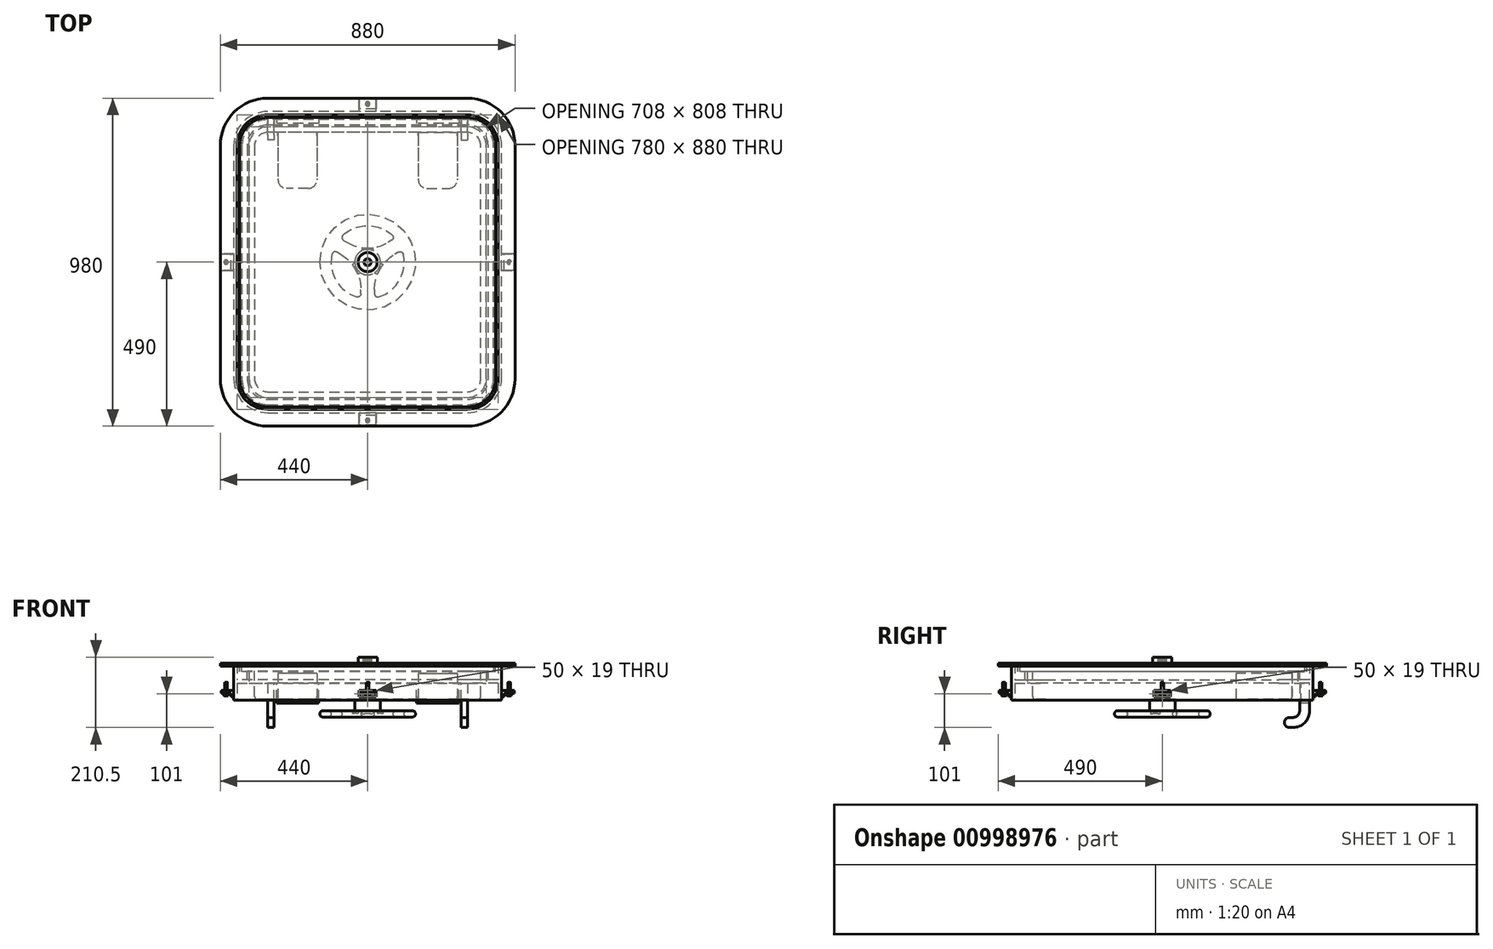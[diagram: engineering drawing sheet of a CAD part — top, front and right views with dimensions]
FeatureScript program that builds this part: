
annotation { "Feature Type Name" : "Feature", "Feature Type Description" : "" }
export const myFeature = defineFeature(function(context is Context, id is Id, definition is map)
    precondition{}
    {
        {
            var Q0;
            Q0=qCreatedBy(makeId("Top.planeOp"),FACE);
            var sketch = newSketch(context, id + "F0", { "sketchPlane" : qUnion([Q0])});
            skLineSegment(sketch, "E0.bottom", {"start": v(-298.4, -450) * mm, "end": v(298.4, -450) * mm});
            skLineSegment(sketch, "E0.top", {"start": v(-298.4, 450) * mm, "end": v(298.4, 450) * mm});
            skLineSegment(sketch, "E0.left", {"start": v(-400, -348.4) * mm, "end": v(-400, 348.4) * mm});
            skLineSegment(sketch, "E0.right", {"start": v(400, -348.4) * mm, "end": v(400, 348.4) * mm});
            skPoint(sketch, "E0.middle", {"position": v(0, 0) * mm});
            skPoint(sketch, "E1.visualSharp", {"position": v(-400, 450) * mm});
            skArc(sketch, "E1.filletArc", {"start": v(-298.4, 450) * mm, "mid": v(-370.24, 420.24) * mm, "end": v(-400, 348.4) * mm});
            skPoint(sketch, "E2.visualSharp", {"position": v(400, 450) * mm});
            skArc(sketch, "E2.filletArc", {"start": v(400, 348.4) * mm, "mid": v(370.24, 420.24) * mm, "end": v(298.4, 450) * mm});
            skPoint(sketch, "E3.visualSharp", {"position": v(400, -450) * mm});
            skArc(sketch, "E3.filletArc", {"start": v(298.4, -450) * mm, "mid": v(370.24, -420.24) * mm, "end": v(400, -348.4) * mm});
            skPoint(sketch, "E4.visualSharp", {"position": v(-400, -450) * mm});
            skArc(sketch, "E4.filletArc", {"start": v(-400, -348.4) * mm, "mid": v(-370.24, -420.24) * mm, "end": v(-298.4, -450) * mm});
            skSolve(sketch);
        }
        {
            var Q0;
            Q0=qCreatedBy(makeId("Front.planeOp"),FACE);
            var sketch = newSketch(context, id + "F1", { "sketchPlane" : qUnion([Q0])});
            skLineSegment(sketch, "E5", {"start": v(-400, 0) * mm, "end": v(-440, 0) * mm});
            skLineSegment(sketch, "E6", {"start": v(-440, 0) * mm, "end": v(-440, 8) * mm});
            skLineSegment(sketch, "E7", {"start": v(-440, 8) * mm, "end": v(-390, 8) * mm});
            skLineSegment(sketch, "E8", {"start": v(-390, 8) * mm, "end": v(-390, -41) * mm});
            skLineSegment(sketch, "E9", {"start": v(-390, -41) * mm, "end": v(-360, -41) * mm});
            skLineSegment(sketch, "E10", {"start": v(-360, -41) * mm, "end": v(-360, -16) * mm});
            skLineSegment(sketch, "E11", {"start": v(-360, -16) * mm, "end": v(-354, -16) * mm});
            skLineSegment(sketch, "E12", {"start": v(-354, -16) * mm, "end": v(-354, -51) * mm});
            skLineSegment(sketch, "E13", {"start": v(-354, -51) * mm, "end": v(-390, -51) * mm});
            skLineSegment(sketch, "E14", {"start": v(-390, -51) * mm, "end": v(-390, -102) * mm});
            skLineSegment(sketch, "E15", {"start": v(-390, -102) * mm, "end": v(-400, -102) * mm});
            skLineSegment(sketch, "E16", {"start": v(-400, -102) * mm, "end": v(-400, 0) * mm});
            skSolve(sketch);
        }
        {
            var Q0;
            Q0=makeQuery(id+"F1.imprint","IMPRINT",FACE,{"disambiguationData":[TD([[makeQuery(id+"F1.imprint","IMPRINT",EDGE,{"derivedFrom":sQuery(id+"F1.wireOp",EDGE,"E5")}),-1.0]])]});
            var Q1;
            Q1=sQuery(id+"F0.wireOp",EDGE,"E0.left");
            var Q2;
            Q2=sQuery(id+"F0.wireOp",EDGE,"E1.filletArc");
            var Q3;
            Q3=sQuery(id+"F0.wireOp",EDGE,"E0.top");
            var Q4;
            Q4=sQuery(id+"F0.wireOp",EDGE,"E2.filletArc");
            var Q5;
            Q5=sQuery(id+"F0.wireOp",EDGE,"E0.right");
            var Q6;
            Q6=sQuery(id+"F0.wireOp",EDGE,"E3.filletArc");
            var Q7;
            Q7=sQuery(id+"F0.wireOp",EDGE,"E0.bottom");
            var Q8;
            Q8=sQuery(id+"F0.wireOp",EDGE,"E4.filletArc");
            sweep(context, id + "F2", {"profiles" : qUnion([Q0]), "path" : qUnion([Q1, Q2, Q3, Q4, Q5, Q6, Q7, Q8])});
        }
        {
            var Q0;
            Q0=makeQuery(id+"F2.opSweep","SWEPT_FACE",FACE,{"disambiguationData":[OSD([sQuery(id+"F0.wireOp",EDGE,"E0.left"),sQuery(id+"F1.wireOp",EDGE,"E7")])]});
            var sketch = newSketch(context, id + "F3", { "sketchPlane" : qUnion([Q0])});
            skLineSegment(sketch, "E17.0", {"start": v(298.4, 432) * mm, "end": v(-298.4, 432) * mm});
            skArc(sketch, "E17.1", {"start": v(382, 348.4) * mm, "mid": v(357.51, 407.51) * mm, "end": v(298.4, 432) * mm});
            skArc(sketch, "E17.2", {"start": v(-298.4, 432) * mm, "mid": v(-357.51, 407.51) * mm, "end": v(-382, 348.4) * mm});
            skLineSegment(sketch, "E17.3", {"start": v(382, -348.4) * mm, "end": v(382, 348.4) * mm});
            skLineSegment(sketch, "E17.4", {"start": v(-382, 348.4) * mm, "end": v(-382, -348.4) * mm});
            skArc(sketch, "E17.5", {"start": v(-382, -348.4) * mm, "mid": v(-357.51, -407.51) * mm, "end": v(-298.4, -432) * mm});
            skLineSegment(sketch, "E17.6", {"start": v(-298.4, -432) * mm, "end": v(298.4, -432) * mm});
            skArc(sketch, "E17.7", {"start": v(298.4, -432) * mm, "mid": v(357.51, -407.51) * mm, "end": v(382, -348.4) * mm});
            skSolve(sketch);
        }
        {
            var Q0;
            Q0=qSketchRegion(id+"F3",true);
            extrude(context, id + "F4", {"entities" : qUnion([Q0]), "oppositeDirection" : true, "depth" : 25 * mm, "offsetDistance" : 25 * mm});
        }
        {
            var Q0;
            Q0=makeQuery(id+"F4.opExtrude","CAP_FACE",FACE,{"disambiguationData":[OSD([sQuery(id+"F3.wireOp",EDGE,"E17.0"),sQuery(id+"F3.wireOp",EDGE,"E17.1"),sQuery(id+"F3.wireOp",EDGE,"E17.2"),sQuery(id+"F3.wireOp",EDGE,"E17.3"),sQuery(id+"F3.wireOp",EDGE,"E17.4"),sQuery(id+"F3.wireOp",EDGE,"E17.5"),sQuery(id+"F3.wireOp",EDGE,"E17.6"),sQuery(id+"F3.wireOp",EDGE,"E17.7")])],"isStart":false});
            shell(context, id + "F5", {"entities" : qUnion([Q0]), "thickness" : 6.35 * mm});
        }
        {
            var Q0;
            Q0=makeQuery(id+"F4.opExtrude","CAP_EDGE",EDGE,{"disambiguationData":[OSD([sQuery(id+"F3.wireOp",EDGE,"E17.6")])],"isStart":true});
            fillet(context, id + "F6", {"entities" : qUnion([Q0]), "radius" : 12.7 * mm, "tangentPropagation" : true, "allowEdgeOverflow" : false});
        }
        {
            var Q0;
            Q0=makeQuery(id+"F5.opShell","OFFSET_FACE",FACE,{"disambiguationData":[OSD([sQuery(id+"F3.wireOp",EDGE,"E17.0"),sQuery(id+"F3.wireOp",EDGE,"E17.1"),sQuery(id+"F3.wireOp",EDGE,"E17.2"),sQuery(id+"F3.wireOp",EDGE,"E17.3"),sQuery(id+"F3.wireOp",EDGE,"E17.4"),sQuery(id+"F3.wireOp",EDGE,"E17.5"),sQuery(id+"F3.wireOp",EDGE,"E17.6"),sQuery(id+"F3.wireOp",EDGE,"E17.7")])]});
            var sketch = newSketch(context, id + "F7", { "sketchPlane" : qUnion([Q0])});
            skLineSegment(sketch, "E18.0", {"start": v(-337.55, -348.4) * mm, "end": v(-337.55, 348.4) * mm});
            skArc(sketch, "E18.1", {"start": v(-298.4, -387.55) * mm, "mid": v(-326.08, -376.08) * mm, "end": v(-337.55, -348.4) * mm});
            skArc(sketch, "E18.2", {"start": v(-337.55, 348.4) * mm, "mid": v(-326.08, 376.08) * mm, "end": v(-298.4, 387.55) * mm});
            skLineSegment(sketch, "E18.3", {"start": v(298.4, -387.55) * mm, "end": v(-298.4, -387.55) * mm});
            skLineSegment(sketch, "E18.4", {"start": v(-298.4, 387.55) * mm, "end": v(298.4, 387.55) * mm});
            skArc(sketch, "E18.5", {"start": v(298.4, 387.55) * mm, "mid": v(326.08, 376.08) * mm, "end": v(337.55, 348.4) * mm});
            skLineSegment(sketch, "E18.6", {"start": v(337.55, 348.4) * mm, "end": v(337.55, -348.4) * mm});
            skArc(sketch, "E18.7", {"start": v(337.55, -348.4) * mm, "mid": v(326.08, -376.08) * mm, "end": v(298.4, -387.55) * mm});
            skSolve(sketch);
        }
        {
            var Q0;
            Q0=qSketchRegion(id+"F7",true);
            extrude(context, id + "F8", {"entities" : qUnion([Q0]), "operationType" : NewBodyOperationType.ADD, "depth" : 101.6 * mm, "offsetDistance" : 25 * mm});
        }
        {
            var Q0;
            Q0=makeQuery(id+"F8.opExtrude","CAP_EDGE",EDGE,{"disambiguationData":[OSD([sQuery(id+"F7.wireOp",EDGE,"E18.0")])],"isStart":false});
            fillet(context, id + "F9", {"entities" : qUnion([Q0]), "radius" : 10 * mm, "tangentPropagation" : true, "allowEdgeOverflow" : false});
        }
        {
            var Q0;
            Q0=makeQuery(id+"F4.opExtrude","CAP_FACE",FACE,{"disambiguationData":[OSD([sQuery(id+"F3.wireOp",EDGE,"E17.0"),sQuery(id+"F3.wireOp",EDGE,"E17.1"),sQuery(id+"F3.wireOp",EDGE,"E17.2"),sQuery(id+"F3.wireOp",EDGE,"E17.3"),sQuery(id+"F3.wireOp",EDGE,"E17.4"),sQuery(id+"F3.wireOp",EDGE,"E17.5"),sQuery(id+"F3.wireOp",EDGE,"E17.6"),sQuery(id+"F3.wireOp",EDGE,"E17.7")])],"isStart":true});
            var sketch = newSketch(context, id + "F10", { "sketchPlane" : qUnion([Q0])});
            skCircle(sketch, "E19", {"center": v(0, 0) * mm, "radius": 28.6 * mm});
            skSolve(sketch);
        }
        {
            var Q0;
            Q0=qSketchRegion(id+"F10",true);
            extrude(context, id + "F11", {"entities" : qUnion([Q0]), "operationType" : NewBodyOperationType.ADD, "depth" : 19 * mm, "offsetDistance" : 25 * mm});
        }
        {
            var Q0;
            Q0=makeQuery(id+"F11.opExtrude","CAP_FACE",FACE,{"disambiguationData":[OSD([sQuery(id+"F10.wireOp",EDGE,"E19")])],"isStart":false});
            var sketch = newSketch(context, id + "F12", { "sketchPlane" : qUnion([Q0])});
            skLineSegment(sketch, "E20.bottom", {"start": v(8.75, -8.75) * mm, "end": v(3.62, -8.75) * mm});
            skLineSegment(sketch, "E20.top", {"start": v(8.75, 8.75) * mm, "end": v(3.62, 8.75) * mm});
            skLineSegment(sketch, "E20.left", {"start": v(8.75, -8.75) * mm, "end": v(8.75, -3.62) * mm});
            skLineSegment(sketch, "E20.right", {"start": v(-8.75, -8.75) * mm, "end": v(-8.75, -3.62) * mm});
            skPoint(sketch, "E20.middle", {"position": v(0, 0) * mm});
            skLineSegment(sketch, "E21.bottom", {"start": v(12.37, 0) * mm, "end": v(8.75, -3.62) * mm});
            skLineSegment(sketch, "E21.top", {"start": v(0, 12.37) * mm, "end": v(-3.62, 8.75) * mm});
            skLineSegment(sketch, "E21.left", {"start": v(12.37, 0) * mm, "end": v(8.75, 3.62) * mm});
            skLineSegment(sketch, "E21.right", {"start": v(0, -12.37) * mm, "end": v(-3.62, -8.75) * mm});
            skLineSegment(sketch, "E22.trimOffspring", {"start": v(-8.75, 3.62) * mm, "end": v(-12.37, 0) * mm});
            skLineSegment(sketch, "E23.trimOffspring", {"start": v(-8.75, 3.62) * mm, "end": v(-8.75, 8.75) * mm});
            skLineSegment(sketch, "E24.trimOffspring", {"start": v(-8.75, -3.62) * mm, "end": v(-12.37, 0) * mm});
            skLineSegment(sketch, "E25.trimOffspring", {"start": v(3.62, -8.75) * mm, "end": v(0, -12.37) * mm});
            skLineSegment(sketch, "E26.trimOffspring", {"start": v(8.75, 3.62) * mm, "end": v(8.75, 8.75) * mm});
            skLineSegment(sketch, "E27.trimOffspring", {"start": v(3.62, 8.75) * mm, "end": v(0, 12.37) * mm});
            skLineSegment(sketch, "E28.trimOffspring", {"start": v(-3.62, -8.75) * mm, "end": v(-8.75, -8.75) * mm});
            skLineSegment(sketch, "E29.trimOffspring", {"start": v(-3.62, 8.75) * mm, "end": v(-8.75, 8.75) * mm});
            skSolve(sketch);
        }
        {
            var Q0;
            Q0=makeQuery(id+"F12.imprint","IMPRINT",FACE,{"disambiguationData":[TD([[makeQuery(id+"F12.imprint","IMPRINT",EDGE,{"derivedFrom":sQuery(id+"F12.wireOp",EDGE,"E20.bottom")}),-1.0]])]});
            extrude(context, id + "F13", {"entities" : qUnion([Q0]), "operationType" : NewBodyOperationType.REMOVE, "oppositeDirection" : true, "depth" : 19 * mm, "offsetDistance" : 25 * mm});
        }
        {
            var Q0;
            Q0=makeQuery(id+"F8.opExtrude","CAP_FACE",FACE,{"disambiguationData":[OSD([sQuery(id+"F7.wireOp",EDGE,"E18.0"),sQuery(id+"F7.wireOp",EDGE,"E18.1"),sQuery(id+"F7.wireOp",EDGE,"E18.2"),sQuery(id+"F7.wireOp",EDGE,"E18.3"),sQuery(id+"F7.wireOp",EDGE,"E18.4"),sQuery(id+"F7.wireOp",EDGE,"E18.5"),sQuery(id+"F7.wireOp",EDGE,"E18.6"),sQuery(id+"F7.wireOp",EDGE,"E18.7")])],"isStart":false});
            var sketch = newSketch(context, id + "F14", { "sketchPlane" : qUnion([Q0])});
            skCircle(sketch, "E30", {"center": v(0, 0) * mm, "radius": 38.1 * mm});
            skSolve(sketch);
        }
        {
            var Q0;
            Q0=qSketchRegion(id+"F14",true);
            extrude(context, id + "F15", {"entities" : qUnion([Q0]), "operationType" : NewBodyOperationType.ADD, "depth" : 33.3 * mm, "offsetDistance" : 25 * mm});
        }
        {
            var Q0;
            Q0=makeQuery(id+"F15.opExtrude","CAP_FACE",FACE,{"disambiguationData":[OSD([sQuery(id+"F14.wireOp",EDGE,"E30")])],"isStart":false});
            var sketch = newSketch(context, id + "F16", { "sketchPlane" : qUnion([Q0])});
            skCircle(sketch, "E31", {"center": v(0, 0) * mm, "radius": 143 * mm});
            skArc(sketch, "E32.0", {"start": v(-33.03, 103.87) * mm, "mid": v(-94.3, 54.66) * mm, "end": v(-106.55, -22.98) * mm});
            skLineSegment(sketch, "E33", {"start": v(-20, 94.35) * mm, "end": v(-20, 82.35) * mm});
            skArc(sketch, "E34", {"start": v(-81, -23.3) * mm, "mid": v(-36.34, 21.35) * mm, "end": v(-20, 82.35) * mm});
            skLineSegment(sketch, "E35", {"start": v(-81, -23.3) * mm, "end": v(-91.78, -29.53) * mm});
            skPoint(sketch, "E36.visualSharp", {"position": v(-20, 107.15) * mm});
            skArc(sketch, "E36.filletArc", {"start": v(-20, 94.35) * mm, "mid": v(-24.1, 102.42) * mm, "end": v(-33.03, 103.87) * mm});
            skPoint(sketch, "E37.visualSharp", {"position": v(-102.9, -35.95) * mm});
            skArc(sketch, "E37.filletArc", {"start": v(-106.55, -22.98) * mm, "mid": v(-100.83, -30.01) * mm, "end": v(-91.78, -29.53) * mm});
            skArc(sketch, "E38.1.0", {"start": v(-73.44, -80.54) * mm, "mid": v(-0.18, -109) * mm, "end": v(73.18, -80.79) * mm});
            skArc(sketch, "E38.1.1", {"start": v(-71.7, -64.5) * mm, "mid": v(-76.65, -72.08) * mm, "end": v(-73.44, -80.54) * mm});
            skLineSegment(sketch, "E38.1.2", {"start": v(-71.7, -64.5) * mm, "end": v(-61.31, -58.5) * mm});
            skArc(sketch, "E38.1.3", {"start": v(60.69, -58.5) * mm, "mid": v(-0.31, -42.15) * mm, "end": v(-61.31, -58.5) * mm});
            skLineSegment(sketch, "E38.1.4", {"start": v(60.69, -58.5) * mm, "end": v(71.46, -64.71) * mm});
            skArc(sketch, "E38.1.5", {"start": v(73.18, -80.79) * mm, "mid": v(76.4, -72.31) * mm, "end": v(71.46, -64.71) * mm});
            skArc(sketch, "E38.2.0", {"start": v(106.47, -23.33) * mm, "mid": v(94.49, 54.34) * mm, "end": v(33.37, 103.76) * mm});
            skArc(sketch, "E38.2.1", {"start": v(91.7, -29.85) * mm, "mid": v(100.74, -30.34) * mm, "end": v(106.47, -23.33) * mm});
            skLineSegment(sketch, "E38.2.2", {"start": v(91.7, -29.85) * mm, "end": v(81.31, -23.85) * mm});
            skArc(sketch, "E38.2.3", {"start": v(20.31, 81.8) * mm, "mid": v(36.66, 20.8) * mm, "end": v(81.31, -23.85) * mm});
            skLineSegment(sketch, "E38.2.4", {"start": v(20.31, 81.8) * mm, "end": v(20.31, 94.25) * mm});
            skArc(sketch, "E38.2.5", {"start": v(33.37, 103.76) * mm, "mid": v(24.42, 102.33) * mm, "end": v(20.31, 94.25) * mm});
            skSolve(sketch);
        }
        {
            var Q0;
            Q0=qSketchRegion(id+"F16",true);
            extrude(context, id + "F17", {"entities" : qUnion([Q0]), "operationType" : NewBodyOperationType.ADD, "depth" : 19 * mm, "offsetDistance" : 25 * mm});
        }
        {
            var Q0;
            Q0=makeQuery(id+"F2.opSweep","MID_CAP_VERTEX",VERTEX,{"disambiguationData":[OSD([sQuery(id+"F0.wireOp",EDGE,"E1.filletArc"),sQuery(id+"F1.wireOp",EDGE,"E15"),sQuery(id+"F1.wireOp",EDGE,"E16")])],"capPos":6.0});
            var Q1;
            Q1=makeQuery(id+"F2.opSweep","MID_CAP_VERTEX",VERTEX,{"disambiguationData":[OSD([sQuery(id+"F0.wireOp",EDGE,"E1.filletArc"),sQuery(id+"F1.wireOp",EDGE,"E5"),sQuery(id+"F1.wireOp",EDGE,"E16")])],"capPos":6.0});
            var Q2;
            Q2=makeQuery(id+"F2.opSweep","MID_CAP_VERTEX",VERTEX,{"disambiguationData":[OSD([sQuery(id+"F0.wireOp",EDGE,"E1.filletArc"),sQuery(id+"F1.wireOp",EDGE,"E5"),sQuery(id+"F1.wireOp",EDGE,"E6")])],"capPos":6.0});
            cPlane(context, id + "F18", {"entities" : qUnion([Q0, Q1, Q2]), "cplaneType" : CPlaneType.THREE_POINT, "offset" : 25 * mm, "width" : 150 * mm, "height" : 150 * mm});
        }
        {
            var Q0;
            Q0=qCreatedBy(id+"F18.planeOp",FACE);
            var sketch = newSketch(context, id + "F19", { "sketchPlane" : qUnion([Q0])});
            skLineSegment(sketch, "E39.0", {"start": v(440, -133.5) * mm, "end": v(440, -51) * mm});
            skLineSegment(sketch, "E40", {"start": v(440, -51) * mm, "end": v(410, -51) * mm});
            skLineSegment(sketch, "E41", {"start": v(410, -51) * mm, "end": v(410, -133.5) * mm});
            skArc(sketch, "E42", {"start": v(390, -153.5) * mm, "mid": v(404.14, -147.64) * mm, "end": v(410, -133.5) * mm});
            skLineSegment(sketch, "E43", {"start": v(379.7, -183.5) * mm, "end": v(390, -183.5) * mm});
            skArc(sketch, "E44", {"start": v(390, -183.5) * mm, "mid": v(425.36, -168.86) * mm, "end": v(440, -133.5) * mm});
            skLineSegment(sketch, "E45", {"start": v(390, -153.5) * mm, "end": v(379.7, -153.5) * mm});
            skArc(sketch, "E46", {"start": v(379.7, -153.5) * mm, "mid": v(364.7, -168.5) * mm, "end": v(379.7, -183.5) * mm});
            skSolve(sketch);
        }
        {
            var Q0;
            Q0=qSketchRegion(id+"F19",true);
            extrude(context, id + "F20", {"entities" : qUnion([Q0]), "operationType" : NewBodyOperationType.ADD, "depth" : 19 * mm, "offsetDistance" : 25 * mm});
        }
        {
            var Q0;
            Q0=makeQuery(id+"F2.opSweep","MID_CAP_VERTEX",VERTEX,{"disambiguationData":[OSD([sQuery(id+"F0.wireOp",EDGE,"E0.top"),sQuery(id+"F1.wireOp",EDGE,"E15"),sQuery(id+"F1.wireOp",EDGE,"E16")])],"capPos":5.0});
            var Q1;
            Q1=makeQuery(id+"F2.opSweep","MID_CAP_VERTEX",VERTEX,{"disambiguationData":[OSD([sQuery(id+"F0.wireOp",EDGE,"E0.top"),sQuery(id+"F1.wireOp",EDGE,"E5"),sQuery(id+"F1.wireOp",EDGE,"E16")])],"capPos":5.0});
            var Q2;
            Q2=makeQuery(id+"F2.opSweep","MID_CAP_VERTEX",VERTEX,{"disambiguationData":[OSD([sQuery(id+"F0.wireOp",EDGE,"E0.top"),sQuery(id+"F1.wireOp",EDGE,"E5"),sQuery(id+"F1.wireOp",EDGE,"E6")])],"capPos":5.0});
            cPlane(context, id + "F21", {"entities" : qUnion([Q0, Q1, Q2]), "cplaneType" : CPlaneType.THREE_POINT, "offset" : 25 * mm, "width" : 150 * mm, "height" : 150 * mm});
        }
        {
            var Q0;
            Q0=qCreatedBy(id+"F21.planeOp",FACE);
            var sketch = newSketch(context, id + "F22", { "sketchPlane" : qUnion([Q0])});
            skArc(sketch, "E47.0.0", {"start": v(379.7, -153.5) * mm, "mid": v(364.7, -168.5) * mm, "end": v(379.7, -183.5) * mm});
            skLineSegment(sketch, "E47.0.1", {"start": v(379.7, -183.5) * mm, "end": v(390, -183.5) * mm});
            skArc(sketch, "E47.0.2", {"start": v(390, -183.5) * mm, "mid": v(425.36, -168.86) * mm, "end": v(440, -133.5) * mm});
            skLineSegment(sketch, "E47.0.3", {"start": v(440, -133.5) * mm, "end": v(440, -102) * mm});
            skLineSegment(sketch, "E47.0.4", {"start": v(440, -102) * mm, "end": v(440, -51) * mm});
            skLineSegment(sketch, "E47.0.5", {"start": v(440, -51) * mm, "end": v(410, -51) * mm});
            skLineSegment(sketch, "E47.0.6", {"start": v(410, -51) * mm, "end": v(410, -133.5) * mm});
            skArc(sketch, "E47.0.7", {"start": v(410, -133.5) * mm, "mid": v(404.14, -147.64) * mm, "end": v(390, -153.5) * mm});
            skLineSegment(sketch, "E47.0.8", {"start": v(390, -153.5) * mm, "end": v(379.7, -153.5) * mm});
            skSolve(sketch);
        }
        {
            var Q0;
            Q0=qSketchRegion(id+"F22",true);
            extrude(context, id + "F23", {"entities" : qUnion([Q0]), "operationType" : NewBodyOperationType.ADD, "oppositeDirection" : true, "depth" : 19 * mm, "offsetDistance" : 25 * mm});
        }
        {
            var Q0;
            Q0=makeQuery(id+"F8.opExtrude","CAP_FACE",FACE,{"disambiguationData":[OSD([sQuery(id+"F7.wireOp",EDGE,"E18.0"),sQuery(id+"F7.wireOp",EDGE,"E18.1"),sQuery(id+"F7.wireOp",EDGE,"E18.2"),sQuery(id+"F7.wireOp",EDGE,"E18.3"),sQuery(id+"F7.wireOp",EDGE,"E18.4"),sQuery(id+"F7.wireOp",EDGE,"E18.5"),sQuery(id+"F7.wireOp",EDGE,"E18.6"),sQuery(id+"F7.wireOp",EDGE,"E18.7")])],"isStart":false});
            var sketch = newSketch(context, id + "F24", { "sketchPlane" : qUnion([Q0])});
            skLineSegment(sketch, "E48.bottom", {"start": v(-151.55, -387.55) * mm, "end": v(-267.55, -387.55) * mm});
            skLineSegment(sketch, "E48.top", {"start": v(-176.55, -220.55) * mm, "end": v(-242.55, -220.55) * mm});
            skLineSegment(sketch, "E48.left", {"start": v(-151.55, -387.55) * mm, "end": v(-151.55, -245.55) * mm});
            skLineSegment(sketch, "E48.right", {"start": v(-267.55, -387.55) * mm, "end": v(-267.55, -245.55) * mm});
            skPoint(sketch, "E49.visualSharp", {"position": v(-151.55, -220.55) * mm});
            skArc(sketch, "E49.filletArc", {"start": v(-151.55, -245.55) * mm, "mid": v(-158.87, -227.87) * mm, "end": v(-176.55, -220.55) * mm});
            skPoint(sketch, "E50.visualSharp", {"position": v(-267.55, -220.55) * mm});
            skArc(sketch, "E50.filletArc", {"start": v(-242.55, -220.55) * mm, "mid": v(-260.23, -227.87) * mm, "end": v(-267.55, -245.55) * mm});
            skLineSegment(sketch, "E51", {"start": v(0, -377.55) * mm, "end": v(0, -236.86) * mm});
            skLineSegment(sketch, "E52.MirrorCS", {"start": v(151.55, -387.55) * mm, "end": v(267.55, -387.55) * mm});
            skLineSegment(sketch, "E53.MirrorCS", {"start": v(151.55, -387.55) * mm, "end": v(151.55, -245.55) * mm});
            skArc(sketch, "E54.MirrorCS", {"start": v(151.55, -245.55) * mm, "mid": v(158.87, -227.87) * mm, "end": v(176.55, -220.55) * mm});
            skLineSegment(sketch, "E55.MirrorCS", {"start": v(176.55, -220.55) * mm, "end": v(242.55, -220.55) * mm});
            skArc(sketch, "E56.MirrorCS", {"start": v(242.55, -220.55) * mm, "mid": v(260.23, -227.87) * mm, "end": v(267.55, -245.55) * mm});
            skLineSegment(sketch, "E57.MirrorCS", {"start": v(267.55, -387.55) * mm, "end": v(267.55, -245.55) * mm});
            skSolve(sketch);
        }
        {
            var Q0;
            Q0=qSketchRegion(id+"F24",true);
            extrude(context, id + "F25", {"entities" : qUnion([Q0]), "operationType" : NewBodyOperationType.REMOVE, "oppositeDirection" : true, "depth" : 78 * mm, "offsetDistance" : 25 * mm});
        }
        {
            var Q0;
            Q0=makeQuery(id+"F2.opSweep","SWEPT_FACE",FACE,{"disambiguationData":[OSD([sQuery(id+"F0.wireOp",EDGE,"E0.left"),sQuery(id+"F1.wireOp",EDGE,"E13")])]});
            var sketch = newSketch(context, id + "F26", { "sketchPlane" : qUnion([Q0])});
            skLineSegment(sketch, "E58.bottom", {"start": v(-272.55, -440) * mm, "end": v(-146.55, -440) * mm});
            skLineSegment(sketch, "E58.left", {"start": v(-272.55, -440) * mm, "end": v(-272.55, -414.6) * mm});
            skLineSegment(sketch, "E59.bottom", {"start": v(272.55, -440) * mm, "end": v(146.55, -440) * mm});
            skLineSegment(sketch, "E59.left", {"start": v(272.55, -440) * mm, "end": v(272.55, -414.6) * mm});
            skLineSegment(sketch, "E59.right", {"start": v(146.55, -440) * mm, "end": v(146.55, -414.6) * mm});
            skLineSegment(sketch, "E60", {"start": v(-146.55, -440) * mm, "end": v(-146.55, -414.6) * mm});
            skLineSegment(sketch, "E61", {"start": v(-146.55, -414.6) * mm, "end": v(-272.55, -414.6) * mm});
            skLineSegment(sketch, "E62", {"start": v(272.55, -414.6) * mm, "end": v(146.55, -414.6) * mm});
            skSolve(sketch);
        }
        {
            var Q0;
            Q0=qSketchRegion(id+"F26",true);
            extrude(context, id + "F27", {"entities" : qUnion([Q0]), "operationType" : NewBodyOperationType.ADD, "depth" : 60 * mm, "offsetDistance" : 25 * mm});
        }
        {
            var Q0;
            {var subQ0=sQuery(id+"F3.wireOp",EDGE,"E17.4");Q0=makeQuery(id+"F5.opShell","OFFSET_EDGE",EDGE,{"disambiguationData":[OSD([subQ0]),TDD([makeQuery(id+"F4.opExtrude","CAP_EDGE",EDGE,{"disambiguationData":[OSD([subQ0])],"isStart":true})])]});}
            fillet(context, id + "F28", {"entities" : qUnion([Q0]), "radius" : 5 * mm, "tangentPropagation" : true, "allowEdgeOverflow" : false});
        }
        {
            var Q0;
            Q0=makeQuery(id+"F17.opExtrude","CAP_EDGE",EDGE,{"disambiguationData":[OSD([sQuery(id+"F16.wireOp",EDGE,"E38.2.0")])],"isStart":true});
            var Q1;
            Q1=makeQuery(id+"F17.opExtrude","CAP_EDGE",EDGE,{"disambiguationData":[OSD([sQuery(id+"F16.wireOp",EDGE,"E38.2.0")])],"isStart":false});
            var Q2;
            Q2=makeQuery(id+"F17.opExtrude","CAP_EDGE",EDGE,{"disambiguationData":[OSD([sQuery(id+"F16.wireOp",EDGE,"E34")])],"isStart":true});
            var Q3;
            Q3=makeQuery(id+"F17.opExtrude","CAP_EDGE",EDGE,{"disambiguationData":[OSD([sQuery(id+"F16.wireOp",EDGE,"E33")])],"isStart":false});
            var Q4;
            Q4=makeQuery(id+"F17.opExtrude","CAP_EDGE",EDGE,{"disambiguationData":[OSD([sQuery(id+"F16.wireOp",EDGE,"E38.1.3")])],"isStart":false});
            var Q5;
            Q5=makeQuery(id+"F17.opExtrude","CAP_EDGE",EDGE,{"disambiguationData":[OSD([sQuery(id+"F16.wireOp",EDGE,"E38.1.3")])],"isStart":true});
            var Q6;
            Q6=makeQuery(id+"F17.opExtrude","CAP_EDGE",EDGE,{"disambiguationData":[OSD([sQuery(id+"F16.wireOp",EDGE,"E31")])],"isStart":false});
            var Q7;
            Q7=makeQuery(id+"F17.opExtrude","CAP_EDGE",EDGE,{"disambiguationData":[OSD([sQuery(id+"F16.wireOp",EDGE,"E31")])],"isStart":true});
            fillet(context, id + "F29", {"entities" : qUnion([Q0, Q1, Q2, Q3, Q4, Q5, Q6, Q7]), "radius" : 9.5 * mm, "tangentPropagation" : true, "allowEdgeOverflow" : false});
        }
        {
            var Q0;
            Q0=qCreatedBy(makeId("Front.planeOp"),FACE);
            var sketch = newSketch(context, id + "F30", { "sketchPlane" : qUnion([Q0])});
            skLineSegment(sketch, "E63.0", {"start": v(-400, -73) * mm, "end": v(-400, -92) * mm});
            skLineSegment(sketch, "E64", {"start": v(-400, -73) * mm, "end": v(-437.5, -73) * mm});
            skLineSegment(sketch, "E65", {"start": v(-437.5, -73) * mm, "end": v(-437.5, -81) * mm});
            skLineSegment(sketch, "E66", {"start": v(-437.5, -81) * mm, "end": v(-408, -81) * mm});
            skLineSegment(sketch, "E67", {"start": v(-408, -81) * mm, "end": v(-408, -92) * mm});
            skLineSegment(sketch, "E68", {"start": v(-408, -92) * mm, "end": v(-400, -92) * mm});
            skPoint(sketch, "E69.orphan", {"position": v(-400, 0) * mm});
            skPoint(sketch, "E70.orphan", {"position": v(-400, -102) * mm});
            skPoint(sketch, "E71.orphan", {"position": v(400, 0) * mm});
            skLineSegment(sketch, "E72.0", {"start": v(400, -73) * mm, "end": v(400, -92) * mm});
            skLineSegment(sketch, "E73", {"start": v(400, -73) * mm, "end": v(437.5, -73) * mm});
            skLineSegment(sketch, "E74", {"start": v(437.5, -73) * mm, "end": v(437.5, -81) * mm});
            skLineSegment(sketch, "E75", {"start": v(437.5, -81) * mm, "end": v(408, -81) * mm});
            skLineSegment(sketch, "E76", {"start": v(408, -81) * mm, "end": v(408, -92) * mm});
            skLineSegment(sketch, "E77", {"start": v(408, -92) * mm, "end": v(400, -92) * mm});
            skPoint(sketch, "E78.orphan", {"position": v(400, -102) * mm});
            skSolve(sketch);
        }
        {
            var Q0;
            Q0=qSketchRegion(id+"F30",true);
            extrude(context, id + "F31", {"entities" : qUnion([Q0]), "operationType" : NewBodyOperationType.ADD, "depth" : 25 * mm, "offsetDistance" : 25 * mm, "hasSecondDirection" : true, "secondDirectionOppositeDirection" : true, "secondDirectionDepth" : 25 * mm});
        }
        {
            var Q0;
            Q0=qCreatedBy(makeId("Right.planeOp"),FACE);
            var sketch = newSketch(context, id + "F32", { "sketchPlane" : qUnion([Q0])});
            skLineSegment(sketch, "E79.0", {"start": v(-450, -73) * mm, "end": v(-450, -92) * mm});
            skLineSegment(sketch, "E80", {"start": v(-450, -73) * mm, "end": v(-487.5, -73) * mm});
            skLineSegment(sketch, "E81", {"start": v(-487.5, -73) * mm, "end": v(-487.5, -81) * mm});
            skLineSegment(sketch, "E82", {"start": v(-487.5, -81) * mm, "end": v(-458, -81) * mm});
            skLineSegment(sketch, "E83", {"start": v(-458, -81) * mm, "end": v(-458, -92) * mm});
            skLineSegment(sketch, "E84", {"start": v(-458, -92) * mm, "end": v(-450, -92) * mm});
            skPoint(sketch, "E85.orphan", {"position": v(-450, 0) * mm});
            skPoint(sketch, "E86.orphan", {"position": v(-450, -102) * mm});
            skLineSegment(sketch, "E87.0", {"start": v(450, -73) * mm, "end": v(450, -92) * mm});
            skLineSegment(sketch, "E88", {"start": v(450, -92) * mm, "end": v(458, -92) * mm});
            skLineSegment(sketch, "E89", {"start": v(458, -92) * mm, "end": v(458, -81) * mm});
            skLineSegment(sketch, "E90", {"start": v(458, -81) * mm, "end": v(487.5, -81) * mm});
            skLineSegment(sketch, "E91", {"start": v(487.5, -81) * mm, "end": v(487.5, -73) * mm});
            skLineSegment(sketch, "E92", {"start": v(487.5, -73) * mm, "end": v(450, -73) * mm});
            skPoint(sketch, "E92.endSnap0", {"position": v(450, -51) * mm});
            skPoint(sketch, "E93.orphan", {"position": v(450, -102) * mm});
            skPoint(sketch, "E94.orphan", {"position": v(450, 0) * mm});
            skSolve(sketch);
        }
        {
            var Q0;
            Q0=qSketchRegion(id+"F32",true);
            extrude(context, id + "F33", {"entities" : qUnion([Q0]), "operationType" : NewBodyOperationType.ADD, "depth" : 25 * mm, "offsetDistance" : 25 * mm, "hasSecondDirection" : true, "secondDirectionOppositeDirection" : true, "secondDirectionDepth" : 25 * mm});
        }
        {
            var Q0;
            Q0=makeQuery(id+"F33.opExtrude","SWEPT_FACE",FACE,{"disambiguationData":[OSD([sQuery(id+"F32.wireOp",EDGE,"E90")])]});
            var sketch = newSketch(context, id + "F34", { "sketchPlane" : qUnion([Q0])});
            skCircle(sketch, "E95", {"center": v(0, -472.75) * mm, "radius": 6.5 * mm});
            skPoint(sketch, "E95.centerSnap0", {"position": v(25, -472.75) * mm});
            skPoint(sketch, "E95.centerSnap1", {"position": v(0, -487.5) * mm});
            skLineSegment(sketch, "E96", {"start": v(25, 472.75) * mm, "end": v(0, 472.75) * mm});
            skCircle(sketch, "E97", {"center": v(0, 472.75) * mm, "radius": 6.5 * mm});
            skCircle(sketch, "E98", {"center": v(-422.75, 0) * mm, "radius": 6.5 * mm});
            skLineSegment(sketch, "E99", {"start": v(-422.75, 0) * mm, "end": v(-422.75, 25) * mm});
            skLineSegment(sketch, "E100", {"start": v(422.75, 25) * mm, "end": v(422.75, 0) * mm});
            skCircle(sketch, "E101", {"center": v(422.75, 0) * mm, "radius": 6.5 * mm});
            skSolve(sketch);
        }
        {
            var Q0;
            Q0=qSketchRegion(id+"F34",true);
            extrude(context, id + "F35", {"entities" : qUnion([Q0]), "operationType" : NewBodyOperationType.ADD, "depth" : 8 * mm, "offsetDistance" : 25 * mm});
        }
        {
            var Q0;
            Q0=makeQuery(id+"F33.opExtrude","SWEPT_FACE",FACE,{"disambiguationData":[OSD([sQuery(id+"F32.wireOp",EDGE,"E92")])]});
            var sketch = newSketch(context, id + "F36", { "sketchPlane" : qUnion([Q0])});
            skPoint(sketch, "E102.centerSnap0", {"position": v(-25, 468.75) * mm});
            skPoint(sketch, "E102.centerSnap1", {"position": v(0, 487.5) * mm});
            skCircle(sketch, "E103", {"center": v(0, 472.75) * mm, "radius": 4 * mm});
            skCircle(sketch, "E104", {"center": v(0, -472.75) * mm, "radius": 4 * mm});
            skCircle(sketch, "E105", {"center": v(-422.75, 0) * mm, "radius": 4 * mm});
            skCircle(sketch, "E106", {"center": v(422.75, 0) * mm, "radius": 4 * mm});
            skSolve(sketch);
        }
        {
            var Q0;
            Q0=qSketchRegion(id+"F36",true);
            extrude(context, id + "F37", {"entities" : qUnion([Q0]), "operationType" : NewBodyOperationType.ADD, "depth" : 25 * mm, "offsetDistance" : 25 * mm});
        }
        {
            var Q0;
            Q0=makeQuery(id+"F37.opExtrude","CAP_EDGE",EDGE,{"disambiguationData":[OSD([sQuery(id+"F36.wireOp",EDGE,"E105")])],"isStart":false});
            var Q1;
            Q1=makeQuery(id+"F35.opExtrude","CAP_EDGE",EDGE,{"disambiguationData":[OSD([sQuery(id+"F34.wireOp",EDGE,"E98")])],"isStart":false});
            var Q2;
            Q2=makeQuery(id+"F35.opExtrude","CAP_EDGE",EDGE,{"disambiguationData":[OSD([sQuery(id+"F34.wireOp",EDGE,"E95")])],"isStart":false});
            var Q3;
            Q3=makeQuery(id+"F37.opExtrude","CAP_EDGE",EDGE,{"disambiguationData":[OSD([sQuery(id+"F36.wireOp",EDGE,"E103")])],"isStart":false});
            var Q4;
            Q4=makeQuery(id+"F35.opExtrude","CAP_EDGE",EDGE,{"disambiguationData":[OSD([sQuery(id+"F34.wireOp",EDGE,"E101")])],"isStart":false});
            var Q5;
            Q5=makeQuery(id+"F37.opExtrude","CAP_EDGE",EDGE,{"disambiguationData":[OSD([sQuery(id+"F36.wireOp",EDGE,"E106")])],"isStart":false});
            var Q6;
            Q6=makeQuery(id+"F35.opExtrude","CAP_EDGE",EDGE,{"disambiguationData":[OSD([sQuery(id+"F34.wireOp",EDGE,"E97")])],"isStart":false});
            var Q7;
            Q7=makeQuery(id+"F37.opExtrude","CAP_EDGE",EDGE,{"disambiguationData":[OSD([sQuery(id+"F36.wireOp",EDGE,"E104")])],"isStart":false});
            chamfer(context, id + "F38", {"entities" : qUnion([Q0, Q1, Q2, Q3, Q4, Q5, Q6, Q7]), "width" : .7 * mm, "tangentPropagation" : true});
        }
    });
